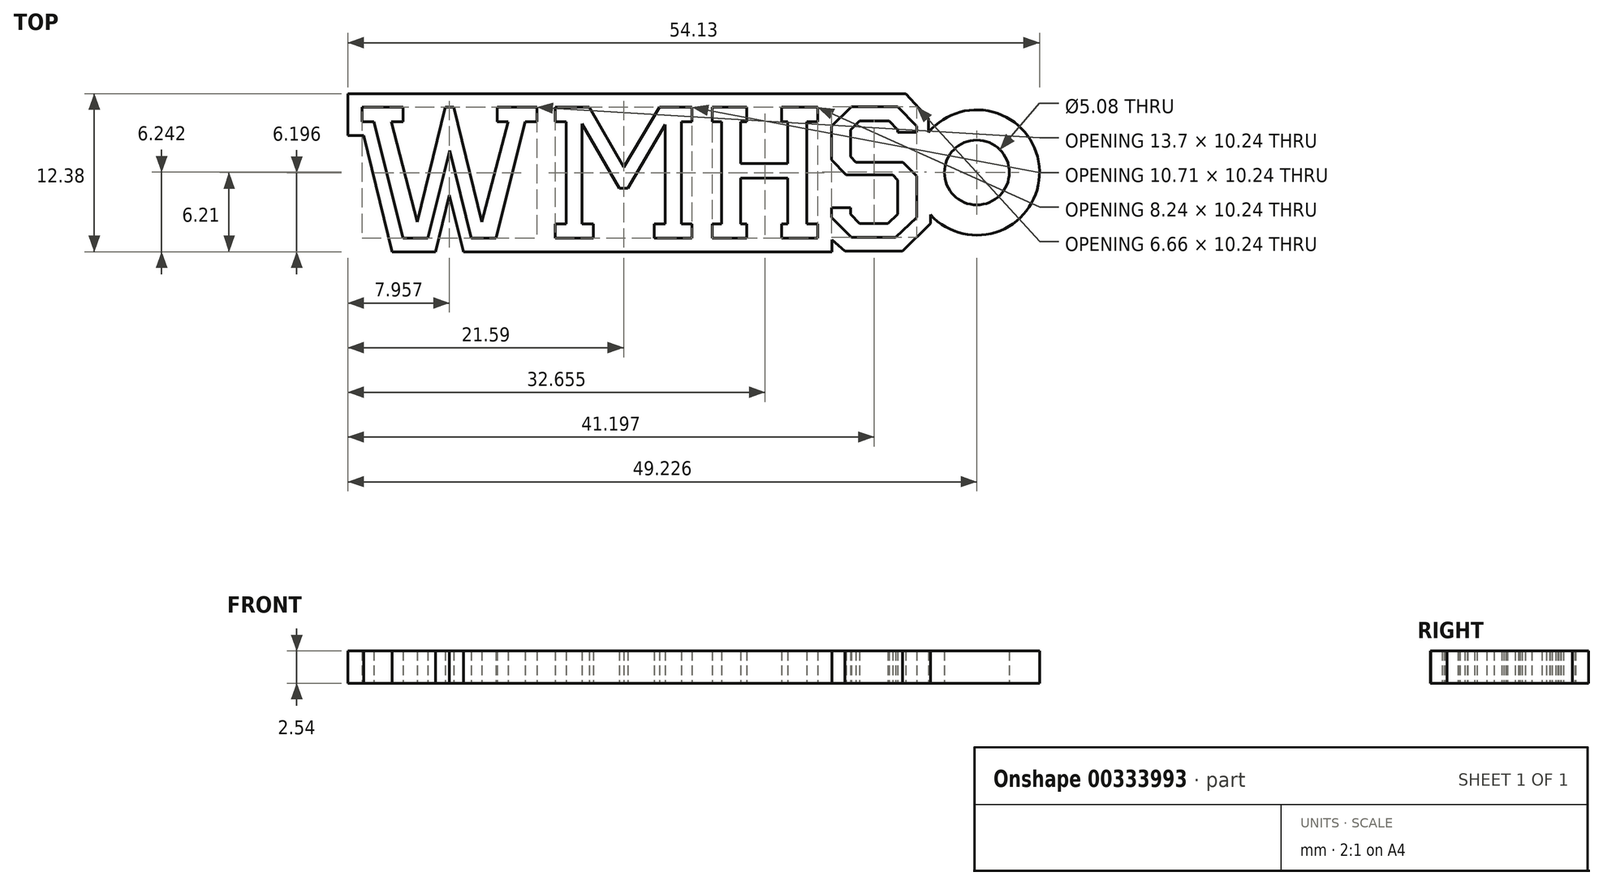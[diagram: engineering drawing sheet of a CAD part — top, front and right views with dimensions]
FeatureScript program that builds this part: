
annotation { "Feature Type Name" : "Feature", "Feature Type Description" : "" }
export const myFeature = defineFeature(function(context is Context, id is Id, definition is map)
    precondition{}
    {
        {
            var Q0;
            Q0=qCreatedBy(makeId("Top.planeOp"),FACE);
            var sketch = newSketch(context, id + "F0", { "sketchPlane" : qUnion([Q0])});
            skLineSegment(sketch, "E0", {"start": v(-10.35, -6.21) * mm, "end": v(-13.73, -6.21) * mm});
            skLineSegment(sketch, "E1", {"start": v(-13.73, -6.21) * mm, "end": v(-14.84, -1.78) * mm});
            skLineSegment(sketch, "E2", {"start": v(-14.84, -1.78) * mm, "end": v(-15.92, -6.21) * mm});
            skLineSegment(sketch, "E3", {"start": v(-15.92, -6.21) * mm, "end": v(-19.33, -6.21) * mm});
            skLineSegment(sketch, "E4", {"start": v(-19.33, -6.21) * mm, "end": v(-21.56, 2.88) * mm});
            skLineSegment(sketch, "E5", {"start": v(-21.56, 2.88) * mm, "end": v(-22.8, 2.88) * mm});
            skLineSegment(sketch, "E6", {"start": v(-22.8, 2.88) * mm, "end": v(-22.8, 6.17) * mm});
            skLineSegment(sketch, "E7", {"start": v(-22.8, 6.17) * mm, "end": v(-17.37, 6.17) * mm});
            skLineSegment(sketch, "E8", {"start": v(-15.92, 6.17) * mm, "end": v(-13.73, 6.17) * mm});
            skLineSegment(sketch, "E9", {"start": v(-12.2, 6.17) * mm, "end": v(-6.9, 6.17) * mm});
            skLineSegment(sketch, "E10", {"start": v(-8, 5.1) * mm, "end": v(-11.1, 5.1) * mm});
            skLineSegment(sketch, "E11", {"start": v(-11.1, 5.1) * mm, "end": v(-11.1, 3.98) * mm});
            skLineSegment(sketch, "E12", {"start": v(-11.1, 3.98) * mm, "end": v(-10.26, 3.98) * mm});
            skLineSegment(sketch, "E13", {"start": v(-10.26, 3.98) * mm, "end": v(-12.3, -3.87) * mm});
            skLineSegment(sketch, "E14", {"start": v(-12.3, -3.87) * mm, "end": v(-14.5, 5.1) * mm});
            skLineSegment(sketch, "E15", {"start": v(-14.5, 5.1) * mm, "end": v(-15.16, 5.1) * mm});
            skLineSegment(sketch, "E16", {"start": v(-15.16, 5.1) * mm, "end": v(-17.37, -3.87) * mm});
            skLineSegment(sketch, "E17", {"start": v(-17.37, -3.87) * mm, "end": v(-19.4, 3.98) * mm});
            skLineSegment(sketch, "E18", {"start": v(-19.4, 3.98) * mm, "end": v(-18.48, 3.98) * mm});
            skLineSegment(sketch, "E19", {"start": v(-18.48, 3.98) * mm, "end": v(-18.48, 5.1) * mm});
            skLineSegment(sketch, "E20", {"start": v(-18.48, 5.1) * mm, "end": v(-21.7, 5.1) * mm});
            skLineSegment(sketch, "E21", {"start": v(-21.7, 5.1) * mm, "end": v(-21.7, 3.98) * mm});
            skLineSegment(sketch, "E22", {"start": v(-21.7, 3.98) * mm, "end": v(-20.76, 3.98) * mm});
            skLineSegment(sketch, "E23", {"start": v(-20.76, 3.98) * mm, "end": v(-18.48, -5.14) * mm});
            skLineSegment(sketch, "E24", {"start": v(-18.48, -5.14) * mm, "end": v(-16.55, -5.14) * mm});
            skLineSegment(sketch, "E25", {"start": v(-16.55, -5.14) * mm, "end": v(-14.82, 1.73) * mm});
            skLineSegment(sketch, "E26", {"start": v(-14.82, 1.73) * mm, "end": v(-13.14, -5.14) * mm});
            skLineSegment(sketch, "E27", {"start": v(-13.14, -5.14) * mm, "end": v(-11.2, -5.14) * mm});
            skLineSegment(sketch, "E28", {"start": v(-11.2, -5.14) * mm, "end": v(-8.9, 3.98) * mm});
            skLineSegment(sketch, "E29", {"start": v(-8.9, 3.98) * mm, "end": v(-8, 3.98) * mm});
            skLineSegment(sketch, "E30", {"start": v(-8, 3.98) * mm, "end": v(-8, 5.1) * mm});
            skLineSegment(sketch, "E31", {"start": v(5.24, -6.21) * mm, "end": v(0.1, -6.21) * mm});
            skLineSegment(sketch, "E32", {"start": v(-2.5, -6.21) * mm, "end": v(-7.66, -6.21) * mm});
            skLineSegment(sketch, "E33", {"start": v(-7.66, 6.17) * mm, "end": v(-3.4, 6.17) * mm});
            skLineSegment(sketch, "E34", {"start": v(1.03, 6.17) * mm, "end": v(5.24, 6.17) * mm});
            skLineSegment(sketch, "E35", {"start": v(4.14, 5.1) * mm, "end": v(1.58, 5.1) * mm});
            skLineSegment(sketch, "E36", {"start": v(1.58, 5.1) * mm, "end": v(-1.2, 0.43) * mm});
            skLineSegment(sketch, "E37", {"start": v(-1.2, 0.43) * mm, "end": v(-3.91, 5.1) * mm});
            skLineSegment(sketch, "E38", {"start": v(-3.91, 5.1) * mm, "end": v(-6.56, 5.1) * mm});
            skLineSegment(sketch, "E39", {"start": v(-6.56, 5.1) * mm, "end": v(-6.56, 3.98) * mm});
            skLineSegment(sketch, "E40", {"start": v(-6.56, 3.98) * mm, "end": v(-5.71, 3.98) * mm});
            skLineSegment(sketch, "E41", {"start": v(-5.71, 3.98) * mm, "end": v(-5.71, -4.04) * mm});
            skLineSegment(sketch, "E42", {"start": v(-5.71, -4.04) * mm, "end": v(-6.56, -4.04) * mm});
            skLineSegment(sketch, "E43", {"start": v(-6.56, -4.04) * mm, "end": v(-6.56, -5.14) * mm});
            skLineSegment(sketch, "E44", {"start": v(-6.56, -5.14) * mm, "end": v(-3.6, -5.14) * mm});
            skLineSegment(sketch, "E45", {"start": v(-3.6, -5.14) * mm, "end": v(-3.6, -4.04) * mm});
            skLineSegment(sketch, "E46", {"start": v(-3.6, -4.04) * mm, "end": v(-4.47, -4.04) * mm});
            skLineSegment(sketch, "E47", {"start": v(-4.47, -4.04) * mm, "end": v(-4.47, 3.83) * mm});
            skLineSegment(sketch, "E48", {"start": v(-4.47, 3.83) * mm, "end": v(-1.54, -1.22) * mm});
            skLineSegment(sketch, "E49", {"start": v(-1.54, -1.22) * mm, "end": v(-0.89, -1.22) * mm});
            skLineSegment(sketch, "E50", {"start": v(-0.89, -1.22) * mm, "end": v(2.05, 3.75) * mm});
            skLineSegment(sketch, "E51", {"start": v(2.05, 3.75) * mm, "end": v(2.05, -4.04) * mm});
            skLineSegment(sketch, "E52", {"start": v(2.05, -4.04) * mm, "end": v(1.2, -4.04) * mm});
            skLineSegment(sketch, "E53", {"start": v(1.2, -4.04) * mm, "end": v(1.2, -5.14) * mm});
            skLineSegment(sketch, "E54", {"start": v(1.2, -5.14) * mm, "end": v(4.14, -5.14) * mm});
            skLineSegment(sketch, "E55", {"start": v(4.14, -5.14) * mm, "end": v(4.14, -4.04) * mm});
            skLineSegment(sketch, "E56", {"start": v(4.14, -4.04) * mm, "end": v(3.3, -4.04) * mm});
            skLineSegment(sketch, "E57", {"start": v(3.3, -4.04) * mm, "end": v(3.3, 3.98) * mm});
            skLineSegment(sketch, "E58", {"start": v(3.3, 3.98) * mm, "end": v(4.14, 3.98) * mm});
            skLineSegment(sketch, "E59", {"start": v(4.14, 3.98) * mm, "end": v(4.14, 5.1) * mm});
            skLineSegment(sketch, "E60", {"start": v(15.08, -6.21) * mm, "end": v(10.04, -6.21) * mm});
            skLineSegment(sketch, "E61", {"start": v(9.52, -6.21) * mm, "end": v(4.5, -6.21) * mm});
            skLineSegment(sketch, "E62", {"start": v(4.5, 6.17) * mm, "end": v(9.52, 6.17) * mm});
            skLineSegment(sketch, "E63", {"start": v(10.04, 6.17) * mm, "end": v(15.07, 6.17) * mm});
            skLineSegment(sketch, "E64", {"start": v(13.97, 5.1) * mm, "end": v(11.14, 5.1) * mm});
            skLineSegment(sketch, "E65", {"start": v(11.14, 5.1) * mm, "end": v(11.14, 3.98) * mm});
            skLineSegment(sketch, "E66", {"start": v(11.14, 3.98) * mm, "end": v(11.62, 3.98) * mm});
            skLineSegment(sketch, "E67", {"start": v(11.62, 3.98) * mm, "end": v(11.62, 0.7) * mm});
            skLineSegment(sketch, "E68", {"start": v(11.62, 0.7) * mm, "end": v(7.94, 0.7) * mm});
            skLineSegment(sketch, "E69", {"start": v(7.94, 0.7) * mm, "end": v(7.94, 3.98) * mm});
            skLineSegment(sketch, "E70", {"start": v(7.94, 3.98) * mm, "end": v(8.4, 3.98) * mm});
            skLineSegment(sketch, "E71", {"start": v(8.4, 3.98) * mm, "end": v(8.4, 5.1) * mm});
            skLineSegment(sketch, "E72", {"start": v(8.4, 5.1) * mm, "end": v(5.74, 5.1) * mm});
            skLineSegment(sketch, "E73", {"start": v(5.74, 5.1) * mm, "end": v(5.74, 3.98) * mm});
            skLineSegment(sketch, "E74", {"start": v(5.74, 3.98) * mm, "end": v(6.44, 3.98) * mm});
            skLineSegment(sketch, "E75", {"start": v(6.44, 3.98) * mm, "end": v(6.44, -4.02) * mm});
            skLineSegment(sketch, "E76", {"start": v(6.44, -4.02) * mm, "end": v(5.74, -4.02) * mm});
            skLineSegment(sketch, "E77", {"start": v(5.74, -4.02) * mm, "end": v(5.74, -5.14) * mm});
            skLineSegment(sketch, "E78", {"start": v(5.74, -5.14) * mm, "end": v(8.4, -5.14) * mm});
            skLineSegment(sketch, "E79", {"start": v(8.4, -5.14) * mm, "end": v(8.4, -4.02) * mm});
            skLineSegment(sketch, "E80", {"start": v(8.4, -4.02) * mm, "end": v(7.94, -4.02) * mm});
            skLineSegment(sketch, "E81", {"start": v(7.94, -4.02) * mm, "end": v(7.94, -0.44) * mm});
            skLineSegment(sketch, "E82", {"start": v(7.94, -0.44) * mm, "end": v(11.62, -0.44) * mm});
            skLineSegment(sketch, "E83", {"start": v(11.62, -0.44) * mm, "end": v(11.62, -4.02) * mm});
            skLineSegment(sketch, "E84", {"start": v(11.62, -4.02) * mm, "end": v(11.14, -4.02) * mm});
            skLineSegment(sketch, "E85", {"start": v(11.14, -4.02) * mm, "end": v(11.14, -5.14) * mm});
            skLineSegment(sketch, "E86", {"start": v(11.14, -5.14) * mm, "end": v(13.97, -5.14) * mm});
            skLineSegment(sketch, "E87", {"start": v(13.97, -5.14) * mm, "end": v(13.97, -4.02) * mm});
            skLineSegment(sketch, "E88", {"start": v(13.97, -4.02) * mm, "end": v(13.12, -4.02) * mm});
            skLineSegment(sketch, "E89", {"start": v(13.12, -4.02) * mm, "end": v(13.12, 3.98) * mm});
            skLineSegment(sketch, "E90", {"start": v(13.12, 3.98) * mm, "end": v(13.97, 3.98) * mm});
            skLineSegment(sketch, "E91", {"start": v(13.97, 3.98) * mm, "end": v(13.97, 5.1) * mm});
            skLineSegment(sketch, "E92", {"start": v(22.8, -3.31) * mm, "end": v(22.8, -4) * mm});
            skLineSegment(sketch, "E93", {"start": v(22.8, -4) * mm, "end": v(20.6, -6.17) * mm});
            skLineSegment(sketch, "E94", {"start": v(20.6, -6.17) * mm, "end": v(16.1, -6.17) * mm});
            skLineSegment(sketch, "E95", {"start": v(20.88, 6.17) * mm, "end": v(22.3, 4.61) * mm});
            skLineSegment(sketch, "E96", {"start": v(22.66, 4.23) * mm, "end": v(22.66, 3.14) * mm});
            skLineSegment(sketch, "E97", {"start": v(21.73, -0.28) * mm, "end": v(20.63, 0.81) * mm});
            skLineSegment(sketch, "E98", {"start": v(20.63, 0.81) * mm, "end": v(16.96, 0.81) * mm});
            skLineSegment(sketch, "E99", {"start": v(16.96, 0.81) * mm, "end": v(16.53, 1.24) * mm});
            skLineSegment(sketch, "E100", {"start": v(16.53, 1.24) * mm, "end": v(16.53, 3.34) * mm});
            skLineSegment(sketch, "E101", {"start": v(16.53, 3.34) * mm, "end": v(17.24, 4.02) * mm});
            skLineSegment(sketch, "E102", {"start": v(17.24, 4.02) * mm, "end": v(19.58, 4.02) * mm});
            skLineSegment(sketch, "E103", {"start": v(19.58, 4.02) * mm, "end": v(20.22, 3.34) * mm});
            skLineSegment(sketch, "E104", {"start": v(20.22, 3.34) * mm, "end": v(20.22, 3.15) * mm});
            skLineSegment(sketch, "E105", {"start": v(20.22, 3.15) * mm, "end": v(21.73, 3.15) * mm});
            skLineSegment(sketch, "E106", {"start": v(21.73, 3.15) * mm, "end": v(21.73, 3.61) * mm});
            skLineSegment(sketch, "E107", {"start": v(21.73, 3.61) * mm, "end": v(20.22, 5.15) * mm});
            skLineSegment(sketch, "E108", {"start": v(20.22, 5.15) * mm, "end": v(16.62, 5.15) * mm});
            skLineSegment(sketch, "E109", {"start": v(16.62, 5.15) * mm, "end": v(15.07, 3.61) * mm});
            skLineSegment(sketch, "E110", {"start": v(15.07, 3.61) * mm, "end": v(15.07, 0.98) * mm});
            skLineSegment(sketch, "E111", {"start": v(15.07, 0.98) * mm, "end": v(16.2, -0.17) * mm});
            skLineSegment(sketch, "E112", {"start": v(16.2, -0.17) * mm, "end": v(19.84, -0.17) * mm});
            skLineSegment(sketch, "E113", {"start": v(19.84, -0.17) * mm, "end": v(20.22, -0.6) * mm});
            skLineSegment(sketch, "E114", {"start": v(20.22, -0.6) * mm, "end": v(20.22, -3.27) * mm});
            skLineSegment(sketch, "E115", {"start": v(20.22, -3.27) * mm, "end": v(19.48, -4) * mm});
            skLineSegment(sketch, "E116", {"start": v(19.48, -4) * mm, "end": v(17.24, -4) * mm});
            skLineSegment(sketch, "E117", {"start": v(17.24, -4) * mm, "end": v(16.53, -3.27) * mm});
            skLineSegment(sketch, "E118", {"start": v(16.53, -3.27) * mm, "end": v(16.53, -2.75) * mm});
            skLineSegment(sketch, "E119", {"start": v(16.53, -2.75) * mm, "end": v(15.07, -2.75) * mm});
            skLineSegment(sketch, "E120", {"start": v(15.07, -2.75) * mm, "end": v(15.07, -3.51) * mm});
            skLineSegment(sketch, "E121", {"start": v(15.07, -3.51) * mm, "end": v(16.62, -5.09) * mm});
            skLineSegment(sketch, "E122", {"start": v(16.62, -5.09) * mm, "end": v(20.08, -5.09) * mm});
            skLineSegment(sketch, "E123", {"start": v(20.08, -5.09) * mm, "end": v(21.73, -3.51) * mm});
            skLineSegment(sketch, "E124", {"start": v(21.73, -3.51) * mm, "end": v(21.73, -0.28) * mm});
            skLineSegment(sketch, "E125", {"start": v(15.08, -6.21) * mm, "end": v(15.08, -5.27) * mm});
            skLineSegment(sketch, "E126", {"start": v(15.08, -5.27) * mm, "end": v(16.1, -6.17) * mm});
            skLineSegment(sketch, "E127", {"start": v(15.07, 6.17) * mm, "end": v(20.88, 6.17) * mm});
            skLineSegment(sketch, "E128", {"start": v(22.3, 4.61) * mm, "end": v(22.66, 4.23) * mm});
            skLineSegment(sketch, "E129", {"start": v(-17.37, 6.17) * mm, "end": v(-15.92, 6.17) * mm});
            skLineSegment(sketch, "E130", {"start": v(-13.73, 6.17) * mm, "end": v(-12.2, 6.17) * mm});
            skLineSegment(sketch, "E131", {"start": v(-3.4, 6.17) * mm, "end": v(1.03, 6.17) * mm});
            skLineSegment(sketch, "E132", {"start": v(9.52, 6.17) * mm, "end": v(10.04, 6.17) * mm});
            skLineSegment(sketch, "E133", {"start": v(-10.35, -6.21) * mm, "end": v(-7.66, -6.21) * mm});
            skLineSegment(sketch, "E134", {"start": v(-2.5, -6.21) * mm, "end": v(0.1, -6.21) * mm});
            skLineSegment(sketch, "E135", {"start": v(9.52, -6.21) * mm, "end": v(10.04, -6.21) * mm});
            skCircle(sketch, "E136", {"center": v(26.43, 0) * mm, "radius": 2.54 * mm});
            skArc(sketch, "E137", {"start": v(22.8, -3.31) * mm, "mid": v(31.33, 0.11) * mm, "end": v(22.66, 3.14) * mm});
            skSolve(sketch);
        }
        {
            var Q0;
            Q0 = qSketchRegion(id + "F0", true);
            extrude(context, id + "F1", {"entities" : qUnion([Q0]), "depth" : 2.54 * mm});
        }
    });
